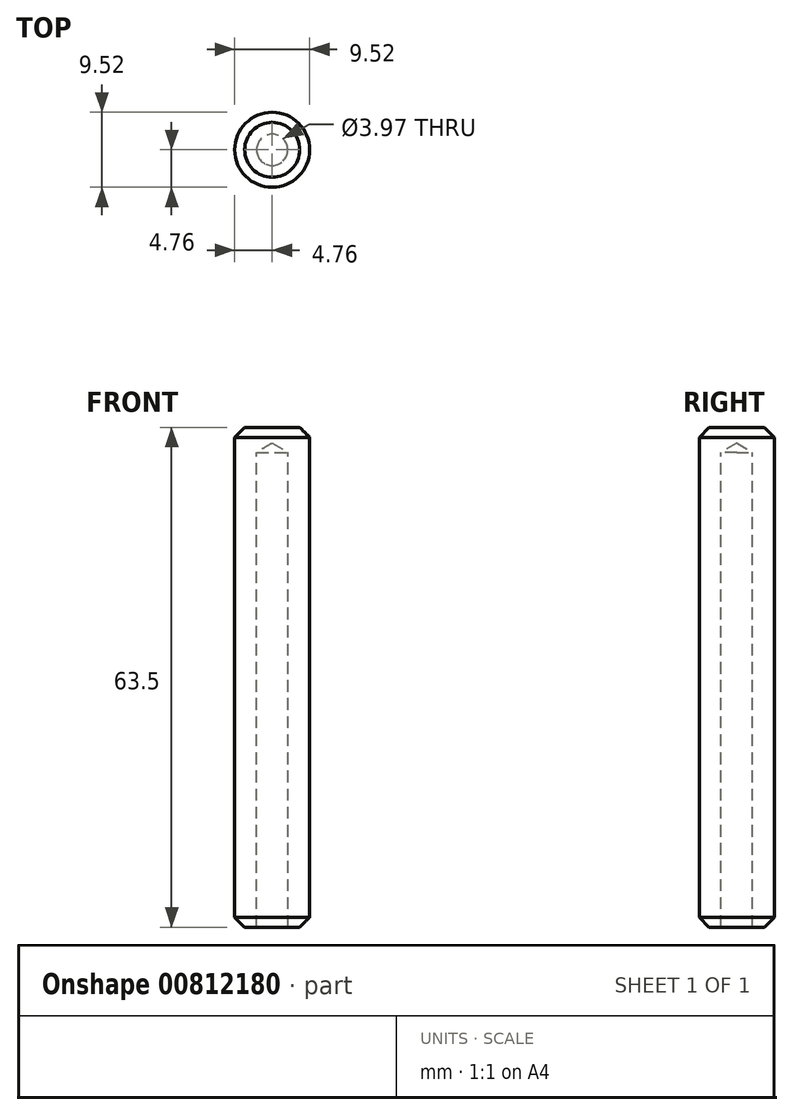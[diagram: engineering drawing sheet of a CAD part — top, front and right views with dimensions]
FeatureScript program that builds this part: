
annotation { "Feature Type Name" : "Feature", "Feature Type Description" : "" }
export const myFeature = defineFeature(function(context is Context, id is Id, definition is map)
    precondition{}
    {
        {
            var Q0;
            Q0=qCreatedBy(makeId("Top.planeOp"),FACE);
            var sketch = newSketch(context, id + "F0", { "sketchPlane" : qUnion([Q0])});
            skCircle(sketch, "E0", {"center": v(0, 0) * mm, "radius": 4.76 * mm});
            skSolve(sketch);
        }
        {
            var Q0;
            Q0=makeQuery(id+"F0.imprint","IMPRINT",FACE,{"disambiguationData":[TD([[makeQuery(id+"F0.imprint","IMPRINT",EDGE,{"derivedFrom":sQuery(id+"F0.wireOp",EDGE,"E0")}),1.0]])]});
            extrude(context, id + "F1", {"entities" : qUnion([Q0]), "depth" : 63.5 * mm, "offsetDistance" : 25.4 * mm});
        }
        {
            var Q0;
            Q0=makeQuery(id+"F1.opExtrude","CAP_EDGE",EDGE,{"disambiguationData":[OSD([sQuery(id+"F0.wireOp",EDGE,"E0")])],"isStart":false});
            var Q1;
            Q1=makeQuery(id+"F1.opExtrude","CAP_EDGE",EDGE,{"disambiguationData":[OSD([sQuery(id+"F0.wireOp",EDGE,"E0")])],"isStart":true});
            chamfer(context, id + "F2", {"entities" : qUnion([Q0, Q1]), "width" : 1.27 * mm, "tangentPropagation" : true});
        }
        {
            var Q0;
            Q0=makeQuery(id+"F1.opExtrude","CAP_FACE",FACE,{"disambiguationData":[OSD([sQuery(id+"F0.wireOp",EDGE,"E0")])],"isStart":true});
            var sketch = newSketch(context, id + "F3", { "sketchPlane" : qUnion([Q0])});
            skPoint(sketch, "E1", {"position": v(0, 0) * mm});
            skSolve(sketch);
        }
        {
            var Q0;
            Q0=sQuery(id+"F3.wireOp",VERTEX,"E1");
            var Q1;
            Q1=makeQuery(id+"F1.opExtrude","SWEPT_BODY",BODY,{"disambiguationData":[OSD([sQuery(id+"F0.wireOp",EDGE,"E0")])]});
            hole(context, id + "F4", {"style" : HoleStyle.SIMPLE, "endStyle" : HoleEndStyle.BLIND, "holeDiameter" : 3.97 * mm, "majorDiameter" : 6.35 * mm, "holeDepth" : 60.32 * mm, "isTappedThrough" : true, "tappedDepth" : 12.7 * mm, "tapClearance" : 3, "locations" : qUnion([Q0]), "scope" : qUnion([Q1]), "startStyle" : HoleStartStyle.SKETCH});
        }
    });
